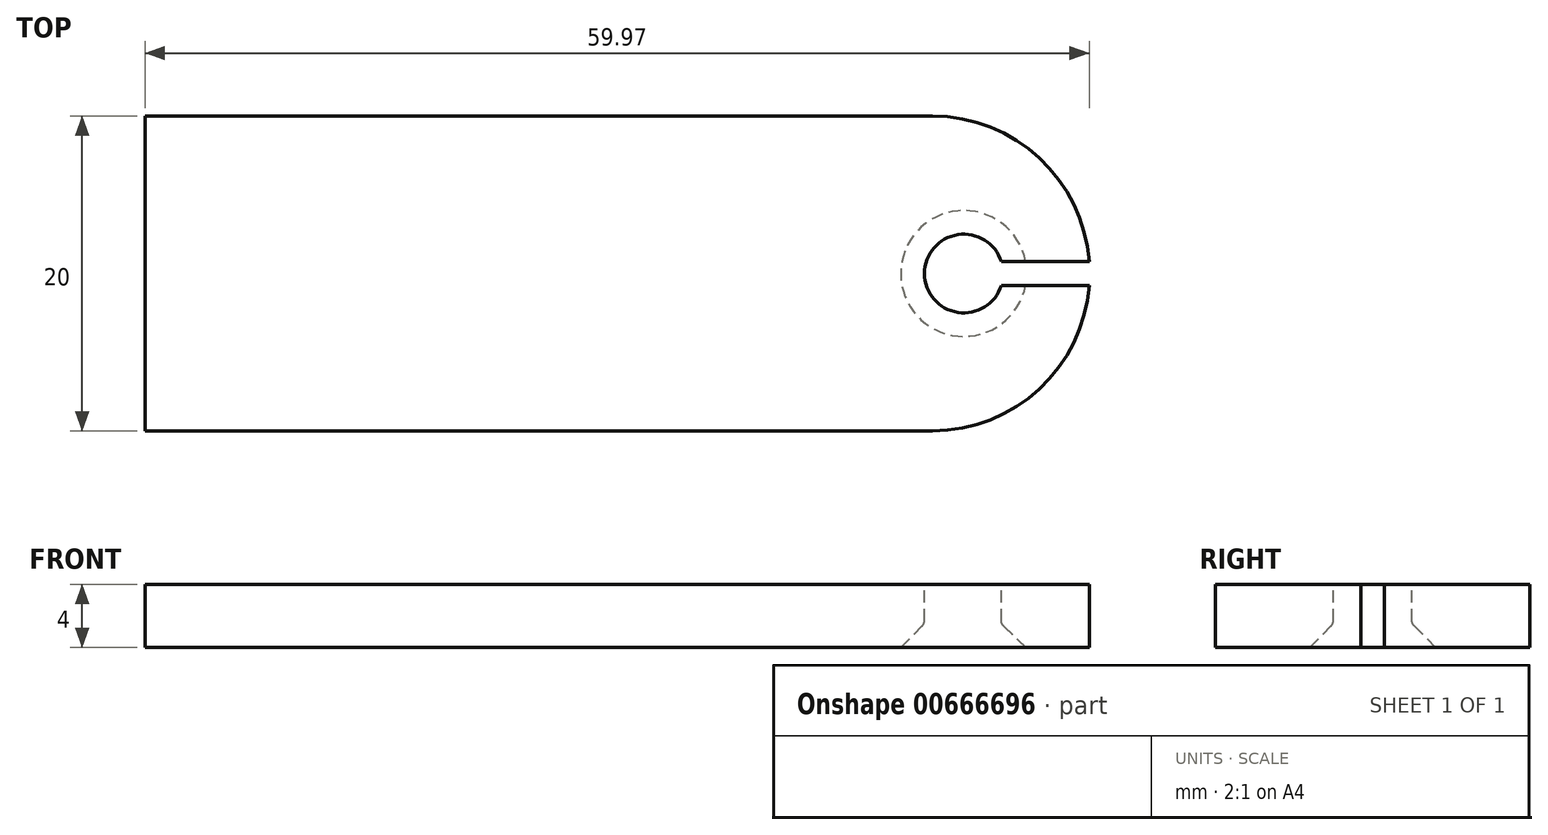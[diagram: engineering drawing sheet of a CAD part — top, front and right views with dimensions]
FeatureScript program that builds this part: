
annotation { "Feature Type Name" : "Feature", "Feature Type Description" : "" }
export const myFeature = defineFeature(function(context is Context, id is Id, definition is map)
    precondition{}
    {
        {
            var Q0;
            Q0=qCreatedBy(makeId("Top.planeOp"),FACE);
            var sketch = newSketch(context, id + "F0", { "sketchPlane" : qUnion([Q0])});
            skLineSegment(sketch, "E0", {"start": v(-16.73, 0) * mm, "end": v(-16.73, 10) * mm});
            skLineSegment(sketch, "E1", {"start": v(-16.73, 10) * mm, "end": v(33.27, 10) * mm});
            skLineSegment(sketch, "E2", {"start": v(-16.73, 0) * mm, "end": v(-16.73, -10) * mm});
            skLineSegment(sketch, "E3", {"start": v(-16.73, -10) * mm, "end": v(33.27, -10) * mm});
            skArc(sketch, "E4", {"start": v(33.27, -10) * mm, "mid": v(43.27, 0) * mm, "end": v(33.27, 10) * mm});
            skSolve(sketch);
        }
        {
            var Q0;
            Q0=makeQuery(id+"F0.imprint","IMPRINT",FACE,{"disambiguationData":[TD([[makeQuery(id+"F0.imprint","IMPRINT",EDGE,{"derivedFrom":sQuery(id+"F0.wireOp",EDGE,"E0")}),-1.0]])]});
            extrude(context, id + "F1", {"entities" : qUnion([Q0]), "depth" : 4 * mm, "offsetDistance" : 25 * mm});
        }
        {
            var Q0;
            Q0=makeQuery(id+"F1.opExtrude","CAP_FACE",FACE,{"disambiguationData":[OSD([sQuery(id+"F0.wireOp",EDGE,"E0"),sQuery(id+"F0.wireOp",EDGE,"E1"),sQuery(id+"F0.wireOp",EDGE,"E2"),sQuery(id+"F0.wireOp",EDGE,"E3"),sQuery(id+"F0.wireOp",EDGE,"E4")])],"isStart":false});
            var sketch = newSketch(context, id + "F2", { "sketchPlane" : qUnion([Q0])});
            skLineSegment(sketch, "E5.bottom", {"start": v(51.27, -0.75) * mm, "end": v(35.27, -0.75) * mm});
            skLineSegment(sketch, "E5.top", {"start": v(51.27, 0.75) * mm, "end": v(35.27, 0.75) * mm});
            skLineSegment(sketch, "E5.left", {"start": v(51.27, -0.75) * mm, "end": v(51.27, 0.75) * mm});
            skLineSegment(sketch, "E5.right", {"start": v(35.27, -0.75) * mm, "end": v(35.27, 0.75) * mm});
            skPoint(sketch, "E5.middle", {"position": v(43.27, 0) * mm});
            skCircle(sketch, "E6", {"center": v(35.27, 0) * mm, "radius": 2.5 * mm});
            skSolve(sketch);
        }
        {
            var Q0;
            {var subQ0=sQuery(id+"F2.wireOp",EDGE,"E6");var subQ1=sQuery(id+"F2.wireOp",EDGE,"E5.bottom");var subQ2=makeQuery(id+"F2.imprint","INTERSECT",VERTEX,{"derivedFrom":[subQ1,subQ0]});Q0=makeQuery(id+"F2.imprint","IMPRINT",FACE,{"disambiguationData":[TD([[makeQuery(id+"F2.imprint","IMPRINT",EDGE,{"disambiguationData":[TD([[subQ2,1.0]])],"derivedFrom":subQ1}),-1.0]])]});}
            var Q1;
            {var subQ0=sQuery(id+"F2.wireOp",EDGE,"E5.right");Q1=makeQuery(id+"F2.imprint","IMPRINT",FACE,{"disambiguationData":[TD([[makeQuery(id+"F2.imprint","IMPRINT",EDGE,{"derivedFrom":subQ0}),1.0]])]});}
            var Q2;
            {var subQ0=sQuery(id+"F2.wireOp",EDGE,"E5.right");Q2=makeQuery(id+"F2.imprint","IMPRINT",FACE,{"disambiguationData":[TD([[makeQuery(id+"F2.imprint","IMPRINT",EDGE,{"derivedFrom":subQ0}),-1.0]])]});}
            extrude(context, id + "F3", {"entities" : qUnion([Q0, Q1, Q2]), "operationType" : NewBodyOperationType.REMOVE, "endBound" : BoundingType.THROUGH_ALL, "oppositeDirection" : true, "depth" : mm, "offsetDistance" : 25 * mm});
        }
        {
            var Q0;
            Q0=makeQuery(id+"F3.boolean.opBoolean","COPY",EDGE,{"derivedFrom":makeQuery(id+"F3.opExtrude","CAP_EDGE",EDGE,{"disambiguationData":[OSD([sQuery(id+"F2.wireOp",EDGE,"E6")])],"isStart":true})});
            var Q1;
            Q1=makeQuery(id+"F3.boolean.opBoolean","INTERSECT",EDGE,{"derivedFrom":[makeQuery(id+"F1.opExtrude","CAP_FACE",FACE,{"disambiguationData":[OSD([sQuery(id+"F0.wireOp",EDGE,"E0"),sQuery(id+"F0.wireOp",EDGE,"E1"),sQuery(id+"F0.wireOp",EDGE,"E2"),sQuery(id+"F0.wireOp",EDGE,"E3"),sQuery(id+"F0.wireOp",EDGE,"E4")])],"isStart":true}),makeQuery(id+"F3.opExtrude","SWEPT_FACE",FACE,{"disambiguationData":[OSD([sQuery(id+"F2.wireOp",EDGE,"E6")])]})]});
            chamfer(context, id + "F4", {"entities" : qUnion([Q0, Q1]), "width" : 1.5 * mm, "tangentPropagation" : true});
        }
        {
            var Q0;
            {var subQ0=sQuery(id+"F2.wireOp",EDGE,"E6");Q0=makeQuery(id+"F4.opChamfer","BLEND_EDGE",EDGE,{"blendedFrom":[makeQuery(id+"F3.boolean.opBoolean","COPY",EDGE,{"derivedFrom":makeQuery(id+"F3.opExtrude","CAP_EDGE",EDGE,{"disambiguationData":[OSD([subQ0])],"isStart":true})}),makeQuery(id+"F3.boolean.opBoolean","COPY",FACE,{"derivedFrom":makeQuery(id+"F3.opExtrude","SWEPT_FACE",FACE,{"disambiguationData":[OSD([subQ0])]})})],"blendedInto":[makeQuery(id+"F3.boolean.opBoolean","COPY",FACE,{"derivedFrom":makeQuery(id+"F3.opExtrude","SWEPT_FACE",FACE,{"disambiguationData":[OSD([subQ0])]})})]});}
            var Q1;
            {var subQ0=makeQuery(id+"F3.opExtrude","SWEPT_FACE",FACE,{"disambiguationData":[OSD([sQuery(id+"F2.wireOp",EDGE,"E6")])]});Q1=makeQuery(id+"F4.opChamfer","BLEND_EDGE",EDGE,{"blendedFrom":[makeQuery(id+"F3.boolean.opBoolean","INTERSECT",EDGE,{"derivedFrom":[makeQuery(id+"F1.opExtrude","CAP_FACE",FACE,{"disambiguationData":[OSD([sQuery(id+"F0.wireOp",EDGE,"E0"),sQuery(id+"F0.wireOp",EDGE,"E1"),sQuery(id+"F0.wireOp",EDGE,"E2"),sQuery(id+"F0.wireOp",EDGE,"E3"),sQuery(id+"F0.wireOp",EDGE,"E4")])],"isStart":true}),subQ0]}),makeQuery(id+"F3.boolean.opBoolean","COPY",FACE,{"derivedFrom":subQ0})],"blendedInto":[makeQuery(id+"F3.boolean.opBoolean","COPY",FACE,{"derivedFrom":subQ0})]});}
            fillet(context, id + "F5", {"entities" : qUnion([Q0, Q1]), "radius" : 0.5 * mm, "tangentPropagation" : true, "allowEdgeOverflow" : false});
        }
    });
